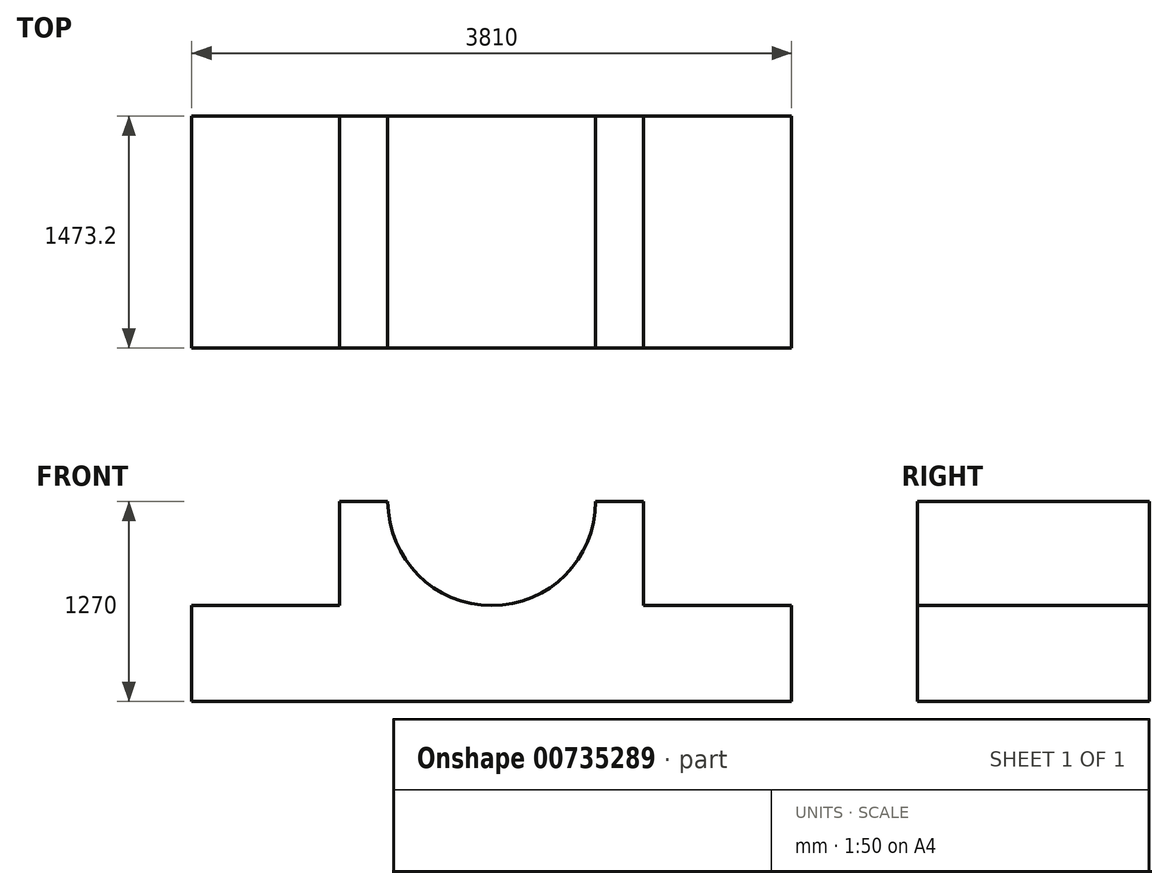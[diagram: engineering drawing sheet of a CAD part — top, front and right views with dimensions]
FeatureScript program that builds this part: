
annotation { "Feature Type Name" : "Feature", "Feature Type Description" : "" }
export const myFeature = defineFeature(function(context is Context, id is Id, definition is map)
    precondition{}
    {
        {
            var Q0;
            Q0=qCreatedBy(makeId("Front.planeOp"),FACE);
            var sketch = newSketch(context, id + "F0", { "sketchPlane" : qUnion([Q0])});
            skLineSegment(sketch, "E0", {"start": v(-70.82, -21.28) * mm, "end": v(3739.18, -21.28) * mm});
            skLineSegment(sketch, "E1", {"start": v(-70.82, -21.28) * mm, "end": v(-70.82, 588.32) * mm});
            skLineSegment(sketch, "E2", {"start": v(-70.82, 588.32) * mm, "end": v(868.98, 588.32) * mm});
            skLineSegment(sketch, "E3", {"start": v(3739.18, -21.28) * mm, "end": v(3739.18, 588.32) * mm});
            skLineSegment(sketch, "E4", {"start": v(3739.18, 588.32) * mm, "end": v(2799.38, 588.32) * mm});
            skLineSegment(sketch, "E5", {"start": v(868.98, 588.32) * mm, "end": v(868.98, 1248.72) * mm});
            skLineSegment(sketch, "E6", {"start": v(2799.38, 588.32) * mm, "end": v(2799.38, 1248.72) * mm});
            skLineSegment(sketch, "E7", {"start": v(2799.38, 1248.72) * mm, "end": v(2494.58, 1248.72) * mm});
            skLineSegment(sketch, "E8", {"start": v(868.98, 1248.72) * mm, "end": v(1173.78, 1248.72) * mm});
            skCircle(sketch, "E9", {"center": v(1834.18, 1248.72) * mm, "radius": 660.4 * mm});
            skSolve(sketch);
        }
        {
            var Q0;
            Q0=makeQuery(id+"F0.imprint","IMPRINT",FACE,{"disambiguationData":[TD([[makeQuery(id+"F0.imprint","IMPRINT",EDGE,{"derivedFrom":sQuery(id+"F0.wireOp",EDGE,"E0")}),1.0]])]});
            extrude(context, id + "F1", {"entities" : qUnion([Q0]), "depth" : 1473.2 * mm, "offsetDistance" : 25.4 * mm});
        }
    });
